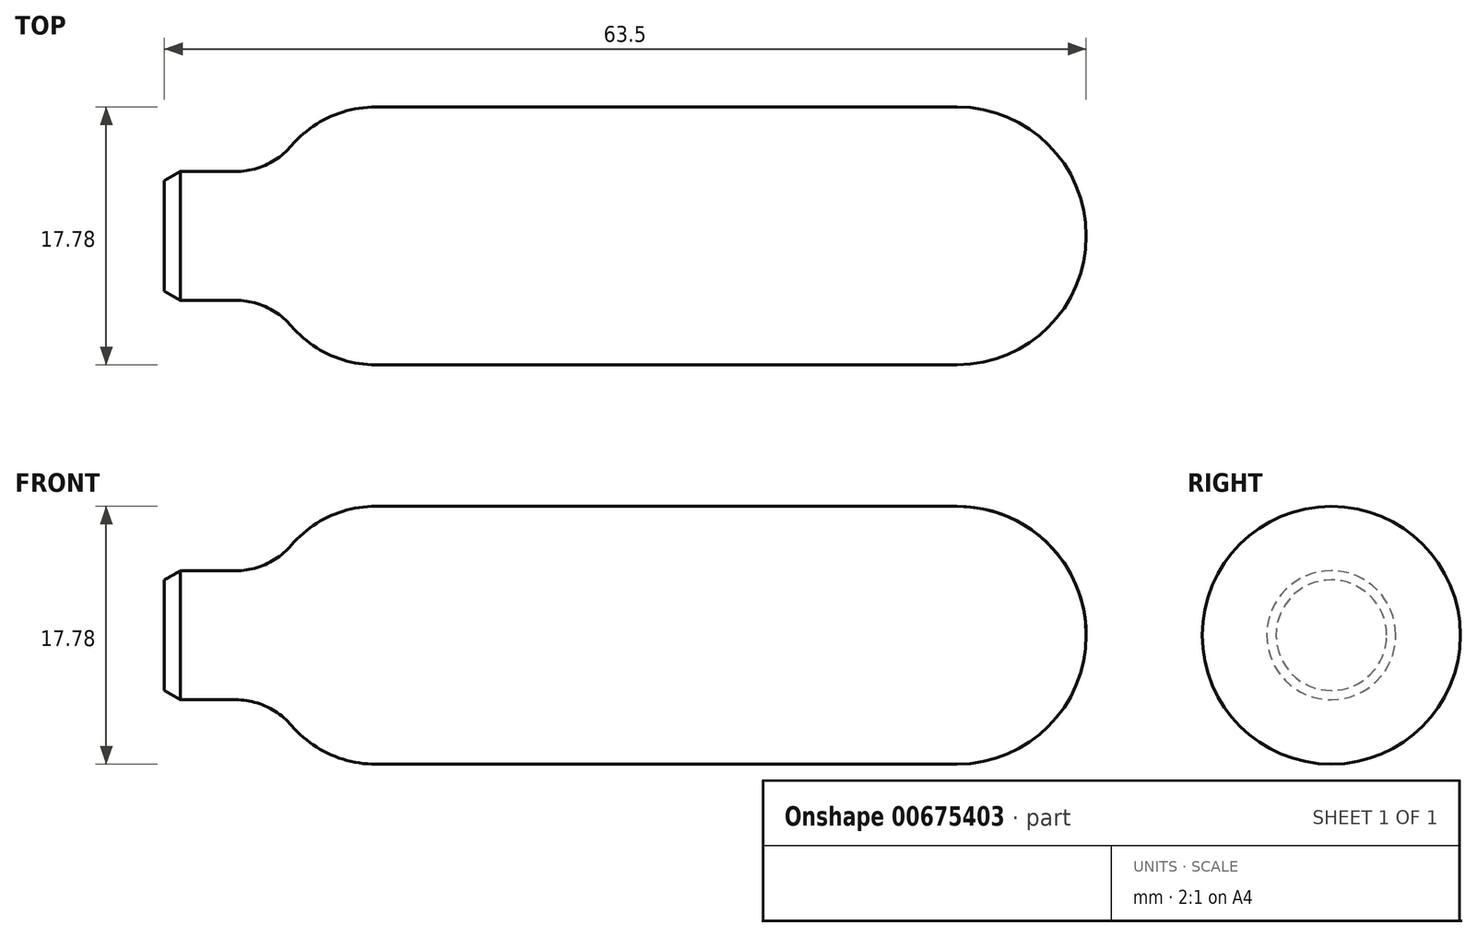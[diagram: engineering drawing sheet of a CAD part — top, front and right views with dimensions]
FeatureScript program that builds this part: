
annotation { "Feature Type Name" : "Feature", "Feature Type Description" : "" }
export const myFeature = defineFeature(function(context is Context, id is Id, definition is map)
    precondition{}
    {
        {
            var Q0;
            Q0=qCreatedBy(makeId("Front.planeOp"),FACE);
            var sketch = newSketch(context, id + "F0", { "sketchPlane" : qUnion([Q0])});
            skLineSegment(sketch, "E0.bottom", {"start": v(-19.96, 0) * mm, "end": v(43.54, 0) * mm});
            skLineSegment(sketch, "E0.top", {"start": v(-12.34, 8.9) * mm, "end": v(43.54, 8.9) * mm});
            skLineSegment(sketch, "E0.left", {"start": v(-19.96, 0) * mm, "end": v(-19.96, 4.45) * mm});
            skLineSegment(sketch, "E0.right", {"start": v(43.54, 0) * mm, "end": v(43.54, 8.89) * mm});
            skLineSegment(sketch, "E1", {"start": v(-19.96, 4.45) * mm, "end": v(-12.34, 4.45) * mm});
            skLineSegment(sketch, "E2", {"start": v(-12.34, 4.44) * mm, "end": v(-12.34, 8.89) * mm});
            skPoint(sketch, "E3.orphan", {"position": v(-19.96, 8.9) * mm});
            skSolve(sketch);
        }
        {
            var Q0;
            Q0=makeQuery(id+"F0.imprint","IMPRINT",FACE,{"disambiguationData":[TD([[makeQuery(id+"F0.imprint","IMPRINT",EDGE,{"derivedFrom":sQuery(id+"F0.wireOp",EDGE,"E0.bottom")}),1.0]])]});
            var Q1;
            Q1=sQuery(id+"F0.wireOp",EDGE,"E0.bottom");
            revolve(context, id + "F1", {"entities" : qUnion([Q0]), "axis" : qUnion([Q1]), "revolveType" : RevolveType.FULL});
        }
        {
            var Q0;
            Q0=makeQuery(id+"F1.opRevolve","SWEPT_FACE",FACE,{"disambiguationData":[OSD([sQuery(id+"F0.wireOp",EDGE,"E0.right")])]});
            fillet(context, id + "F2", {"entities" : qUnion([Q0]), "radius" : 8.9 * mm, "tangentPropagation" : true, "allowEdgeOverflow" : false});
        }
        {
            var Q0;
            Q0=makeQuery(id+"F1.opRevolve","SWEPT_EDGE",EDGE,{"disambiguationData":[OSD([sQuery(id+"F0.wireOp",EDGE,"E0.top"),sQuery(id+"F0.wireOp",EDGE,"E2")])]});
            fillet(context, id + "F3", {"entities" : qUnion([Q0]), "radius" : 7.62 * mm, "tangentPropagation" : true, "allowEdgeOverflow" : false});
        }
        {
            var Q0;
            Q0=makeQuery(id+"F3.opFillet","BLEND_EDGE",EDGE,{"blendedFrom":[makeQuery(id+"F1.opRevolve","SWEPT_EDGE",EDGE,{"disambiguationData":[OSD([sQuery(id+"F0.wireOp",EDGE,"E0.top"),sQuery(id+"F0.wireOp",EDGE,"E2")])]}),makeQuery(id+"F1.opRevolve","SWEPT_FACE",FACE,{"disambiguationData":[OSD([sQuery(id+"F0.wireOp",EDGE,"E1")])]})],"blendedInto":[makeQuery(id+"F1.opRevolve","SWEPT_FACE",FACE,{"disambiguationData":[OSD([sQuery(id+"F0.wireOp",EDGE,"E1")])]})]});
            fillet(context, id + "F4", {"entities" : qUnion([Q0]), "radius" : 5.08 * mm, "tangentPropagation" : true, "allowEdgeOverflow" : false});
        }
        {
            var Q0;
            Q0=makeQuery(id+"F1.opRevolve","SWEPT_EDGE",EDGE,{"disambiguationData":[OSD([sQuery(id+"F0.wireOp",EDGE,"E0.left"),sQuery(id+"F0.wireOp",EDGE,"E1")])]});
            chamfer(context, id + "F5", {"entities" : qUnion([Q0]), "chamferType" : ChamferType.OFFSET_ANGLE, "width" : 0.64 * mm, "oppositeDirection" : false, "angle" : 60 * degree, "tangentPropagation" : true});
        }
    });
